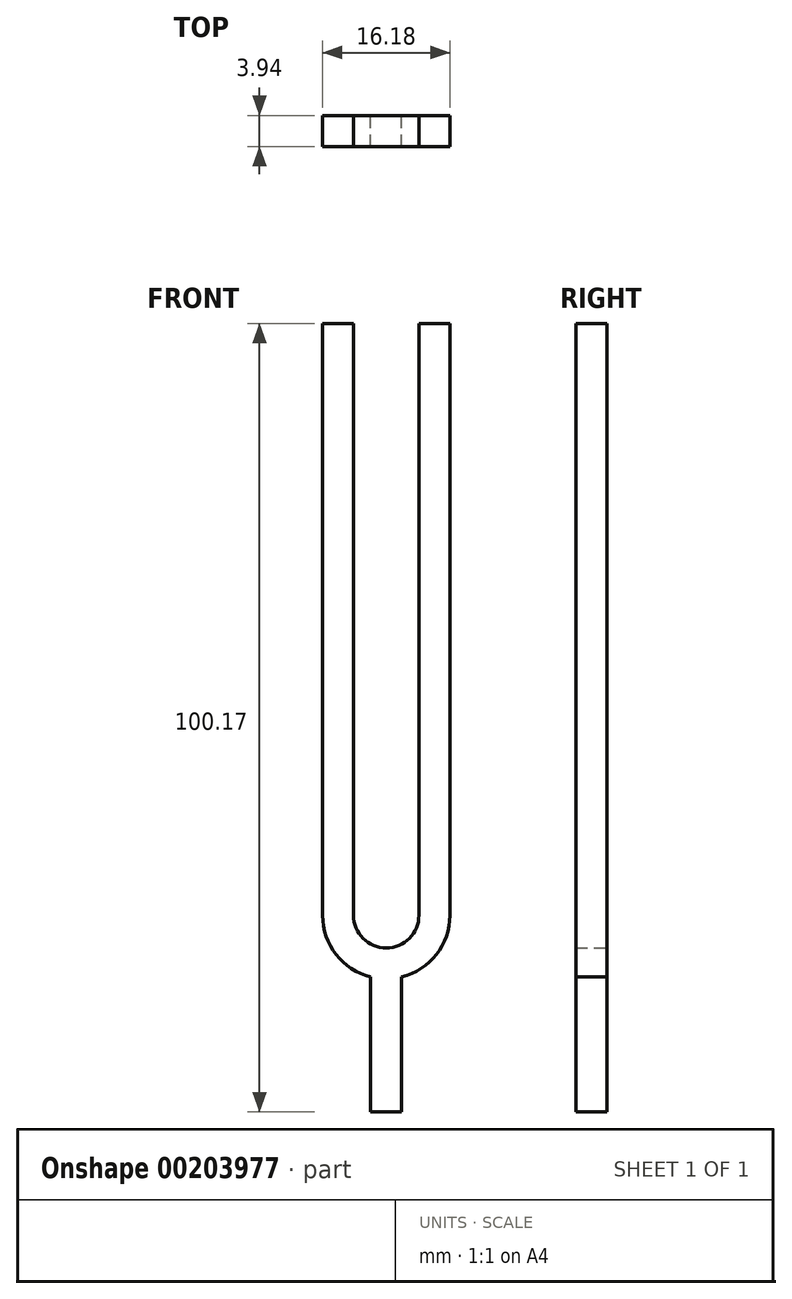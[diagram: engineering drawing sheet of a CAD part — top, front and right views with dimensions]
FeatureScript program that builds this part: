
annotation { "Feature Type Name" : "Feature", "Feature Type Description" : "" }
export const myFeature = defineFeature(function(context is Context, id is Id, definition is map)
    precondition{}
    {
        {
            var Q0;
            Q0=qCreatedBy(makeId("Front.planeOp"),FACE);
            var sketch = newSketch(context, id + "F0", { "sketchPlane" : qUnion([Q0])});
            skLineSegment(sketch, "E0", {"start": v(-8.09, 75.17) * mm, "end": v(-8.09, 0) * mm});
            skArc(sketch, "E1", {"start": v(-8.09, 0) * mm, "mid": v(0, -8.09) * mm, "end": v(8.09, 0) * mm});
            skLineSegment(sketch, "E2", {"start": v(-4.15, 75.17) * mm, "end": v(-4.15, 0) * mm});
            skLineSegment(sketch, "E3", {"start": v(-8.09, 75.17) * mm, "end": v(-4.15, 75.17) * mm});
            skArc(sketch, "E4", {"start": v(-4.15, 0) * mm, "mid": v(0, -4.15) * mm, "end": v(4.15, 0) * mm});
            skLineSegment(sketch, "E5.MirrorCS", {"start": v(4.15, 75.17) * mm, "end": v(4.15, 0) * mm});
            skLineSegment(sketch, "E6.MirrorCS", {"start": v(8.09, 75.17) * mm, "end": v(8.09, 0) * mm});
            skLineSegment(sketch, "E7", {"start": v(4.15, 75.17) * mm, "end": v(8.09, 75.17) * mm});
            skSolve(sketch);
        }
        {
            var Q0;
            Q0 = qSketchRegion(id + "F0", true);
            extrude(context, id + "F1", {"entities" : qUnion([Q0]), "endBound" : BoundingType.SYMMETRIC, "depth" : 3.94 * mm});
        }
        {
            var Q0;
            Q0=qCreatedBy(makeId("Top.planeOp"),FACE);
            cPlane(context, id + "F2", {"entities" : qUnion([Q0]), "cplaneType" : CPlaneType.OFFSET, "offset" : 25 * mm, "oppositeDirection" : true, "width" : 150 * mm, "height" : 150 * mm});
        }
        {
            var Q0;
            Q0=qCreatedBy(id+"F2.planeOp",FACE);
            var sketch = newSketch(context, id + "F3", { "sketchPlane" : qUnion([Q0])});
            skLineSegment(sketch, "E8.bottom", {"start": v(-1.97, -1.97) * mm, "end": v(1.97, -1.97) * mm});
            skLineSegment(sketch, "E8.top", {"start": v(-1.97, 1.97) * mm, "end": v(1.97, 1.97) * mm});
            skLineSegment(sketch, "E8.left", {"start": v(-1.97, -1.97) * mm, "end": v(-1.97, 1.97) * mm});
            skLineSegment(sketch, "E8.right", {"start": v(1.97, -1.97) * mm, "end": v(1.97, 1.97) * mm});
            skPoint(sketch, "E9", {"position": v(0, -1.97) * mm});
            skSolve(sketch);
        }
        {
            var Q0;
            Q0 = qSketchRegion(id + "F3", true);
            extrude(context, id + "F4", {"entities" : qUnion([Q0]), "operationType" : NewBodyOperationType.ADD, "endBound" : BoundingType.UP_TO_NEXT, "depth" : 25 * mm});
        }
    });
